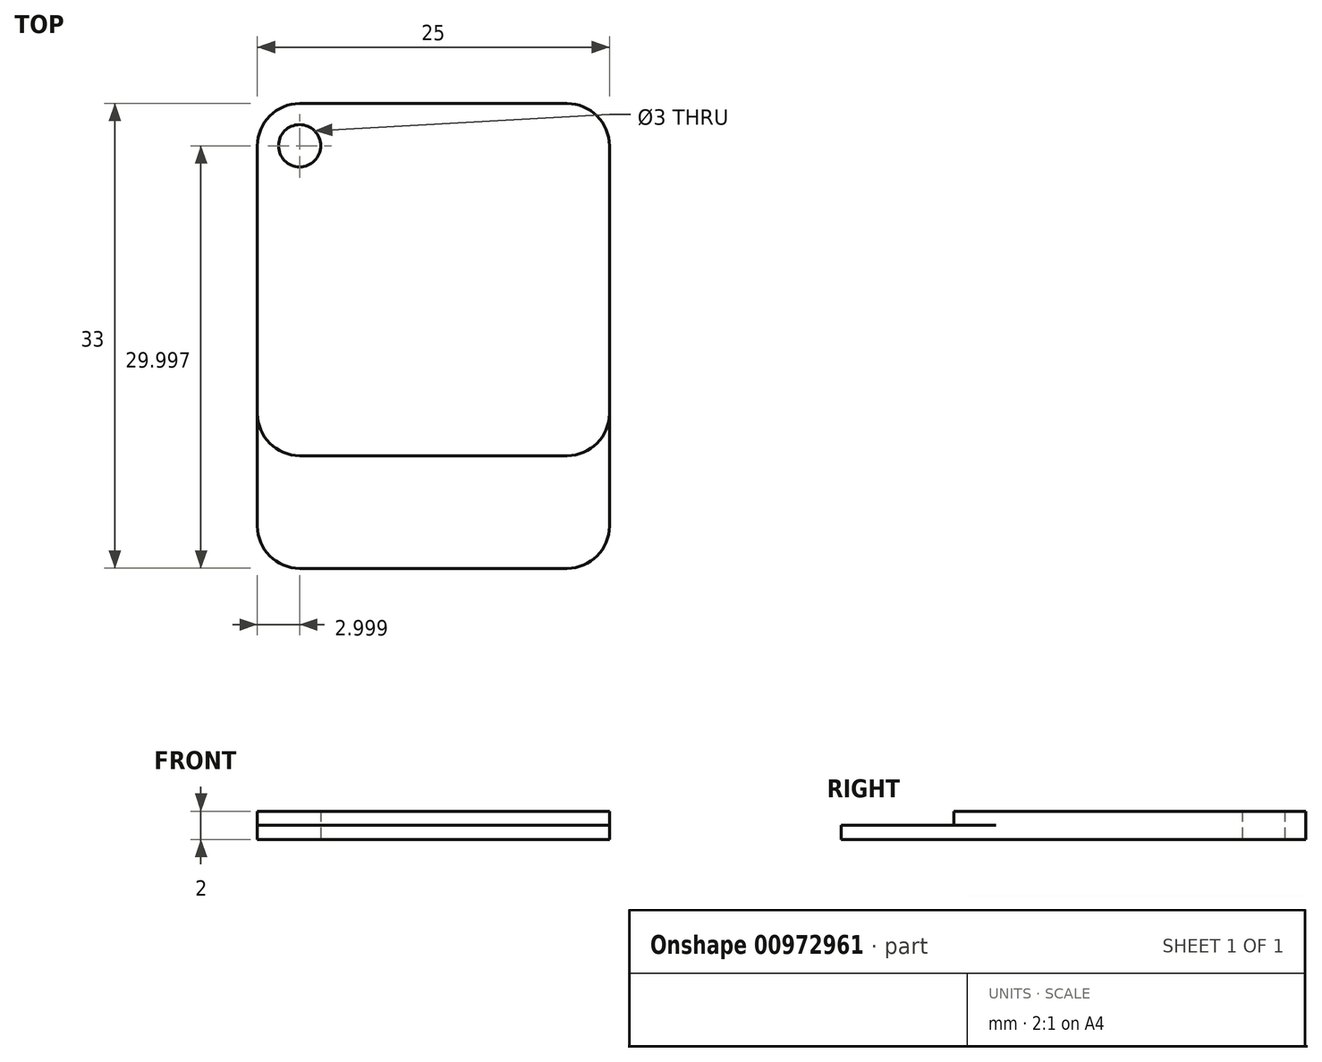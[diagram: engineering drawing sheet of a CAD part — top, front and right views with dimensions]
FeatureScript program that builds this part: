
annotation { "Feature Type Name" : "Feature", "Feature Type Description" : "" }
export const myFeature = defineFeature(function(context is Context, id is Id, definition is map)
    precondition{}
    {
        {
            var Q0;
            Q0=qCreatedBy(makeId("Top.planeOp"),FACE);
            var sketch = newSketch(context, id + "F0", { "sketchPlane" : qUnion([Q0])});
            skLineSegment(sketch, "E0.bottom", {"start": v(-6.97, 7.39) * mm, "end": v(12.03, 7.39) * mm});
            skLineSegment(sketch, "E0.top", {"start": v(-6.97, -25.61) * mm, "end": v(12.03, -25.61) * mm});
            skLineSegment(sketch, "E0.left", {"start": v(-9.97, 4.39) * mm, "end": v(-9.97, -14.61) * mm});
            skLineSegment(sketch, "E0.right", {"start": v(15.03, 4.39) * mm, "end": v(15.03, -14.61) * mm});
            skLineSegment(sketch, "E1", {"start": v(-6.97, -17.61) * mm, "end": v(12.03, -17.61) * mm});
            skPoint(sketch, "E2.visualSharp", {"position": v(-9.97, 7.39) * mm});
            skArc(sketch, "E2.filletArc", {"start": v(-6.97, 7.39) * mm, "mid": v(-9.1, 6.5) * mm, "end": v(-9.97, 4.39) * mm});
            skPoint(sketch, "E3.visualSharp", {"position": v(15.03, 7.39) * mm});
            skArc(sketch, "E3.filletArc", {"start": v(15.03, 4.39) * mm, "mid": v(14.15, 6.5) * mm, "end": v(12.03, 7.39) * mm});
            skPoint(sketch, "E4.visualSharp", {"position": v(15.03, -25.61) * mm});
            skArc(sketch, "E4.filletArc", {"start": v(12.03, -25.61) * mm, "mid": v(14.15, -24.73) * mm, "end": v(15.03, -22.61) * mm});
            skPoint(sketch, "E5.visualSharp", {"position": v(-9.97, -25.61) * mm});
            skArc(sketch, "E5.filletArc", {"start": v(-9.97, -22.61) * mm, "mid": v(-9.1, -24.73) * mm, "end": v(-6.97, -25.61) * mm});
            skArc(sketch, "E6.filletArc", {"start": v(-9.97, -14.61) * mm, "mid": v(-9.1, -16.73) * mm, "end": v(-6.97, -17.61) * mm});
            skArc(sketch, "E7.filletArc", {"start": v(12.03, -17.61) * mm, "mid": v(14.15, -16.73) * mm, "end": v(15.03, -14.61) * mm});
            skLineSegment(sketch, "E8", {"start": v(-9.97, -14.61) * mm, "end": v(-9.97, -22.61) * mm});
            skLineSegment(sketch, "E9", {"start": v(15.03, -14.61) * mm, "end": v(15.03, -22.61) * mm});
            skCircle(sketch, "E10", {"center": v(-6.97, 4.39) * mm, "radius": 1.5 * mm});
            skSolve(sketch);
        }
        {
            var Q0;
            Q0=makeQuery(id+"F0.imprint","IMPRINT",FACE,{"disambiguationData":[TD([[makeQuery(id+"F0.imprint","IMPRINT",EDGE,{"derivedFrom":sQuery(id+"F0.wireOp",EDGE,"E0.bottom")}),-1.0]])]});
            extrude(context, id + "F1", {"entities" : qUnion([Q0]), "depth" : 2 * mm, "offsetDistance" : 25 * mm});
        }
        {
            var Q0;
            Q0=makeQuery(id+"F0.imprint","IMPRINT",FACE,{"disambiguationData":[TD([[makeQuery(id+"F0.imprint","IMPRINT",EDGE,{"derivedFrom":sQuery(id+"F0.wireOp",EDGE,"E0.top")}),1.0]])]});
            extrude(context, id + "F2", {"entities" : qUnion([Q0]), "operationType" : NewBodyOperationType.ADD, "depth" : 1 * mm, "offsetDistance" : 25 * mm});
        }
        {
            var Q0;
            Q0=makeQuery(id+"F1.opExtrude","CAP_FACE",FACE,{"disambiguationData":[OSD([sQuery(id+"F0.wireOp",EDGE,"E0.bottom"),sQuery(id+"F0.wireOp",EDGE,"E0.left"),sQuery(id+"F0.wireOp",EDGE,"E0.right"),sQuery(id+"F0.wireOp",EDGE,"E1"),sQuery(id+"F0.wireOp",EDGE,"E2.filletArc"),sQuery(id+"F0.wireOp",EDGE,"E3.filletArc"),sQuery(id+"F0.wireOp",EDGE,"E6.filletArc"),sQuery(id+"F0.wireOp",EDGE,"E7.filletArc"),sQuery(id+"F0.wireOp",EDGE,"E10")])],"isStart":false});
            cPlane(context, id + "F3", {"entities" : qUnion([Q0]), "cplaneType" : CPlaneType.OFFSET, "offset" : 0 * mm, "width" : 150 * mm, "height" : 150 * mm});
        }
    });
